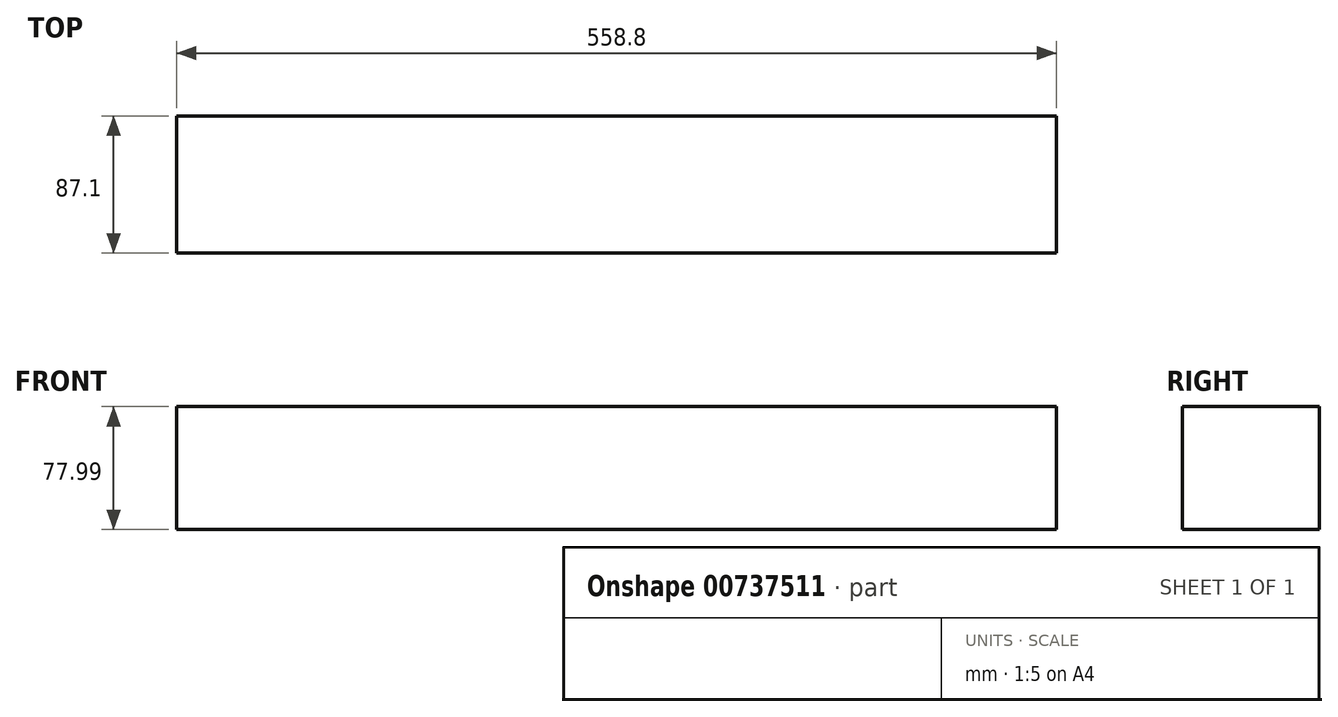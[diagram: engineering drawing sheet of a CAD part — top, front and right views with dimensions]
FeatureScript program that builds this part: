
annotation { "Feature Type Name" : "Feature", "Feature Type Description" : "" }
export const myFeature = defineFeature(function(context is Context, id is Id, definition is map)
    precondition{}
    {
        {
            var Q0;
            Q0=qCreatedBy(makeId("Right.planeOp"),FACE);
            var sketch = newSketch(context, id + "F0", { "sketchPlane" : qUnion([Q0])});
            skLineSegment(sketch, "E0.bottom", {"start": v(-45.07, 41.02) * mm, "end": v(42.03, 41.02) * mm});
            skLineSegment(sketch, "E0.top", {"start": v(-45.07, -36.97) * mm, "end": v(42.03, -36.97) * mm});
            skLineSegment(sketch, "E0.left", {"start": v(-45.07, 41.02) * mm, "end": v(-45.07, -36.97) * mm});
            skLineSegment(sketch, "E0.right", {"start": v(42.03, 41.02) * mm, "end": v(42.03, -36.97) * mm});
            skSolve(sketch);
        }
        {
            var Q0;
            Q0=makeQuery(id+"F0.imprint","IMPRINT",FACE,{"disambiguationData":[TD([[makeQuery(id+"F0.imprint","IMPRINT",EDGE,{"derivedFrom":sQuery(id+"F0.wireOp",EDGE,"E0.bottom")}),-1.0]])]});
            extrude(context, id + "F1", {"entities" : qUnion([Q0]), "oppositeDirection" : true, "depth" : 279.4 * mm, "offsetDistance" : 25.4 * mm});
        }
        {
            var Q0;
            Q0=makeQuery(id+"F1.opExtrude","CAP_FACE",FACE,{"disambiguationData":[OSD([sQuery(id+"F0.wireOp",EDGE,"E0.bottom"),sQuery(id+"F0.wireOp",EDGE,"E0.top"),sQuery(id+"F0.wireOp",EDGE,"E0.left"),sQuery(id+"F0.wireOp",EDGE,"E0.right")])],"isStart":true});
            extrude(context, id + "F2", {"entities" : qUnion([Q0]), "operationType" : NewBodyOperationType.ADD, "depth" : 279.4 * mm, "offsetDistance" : 25.4 * mm});
        }
    });
